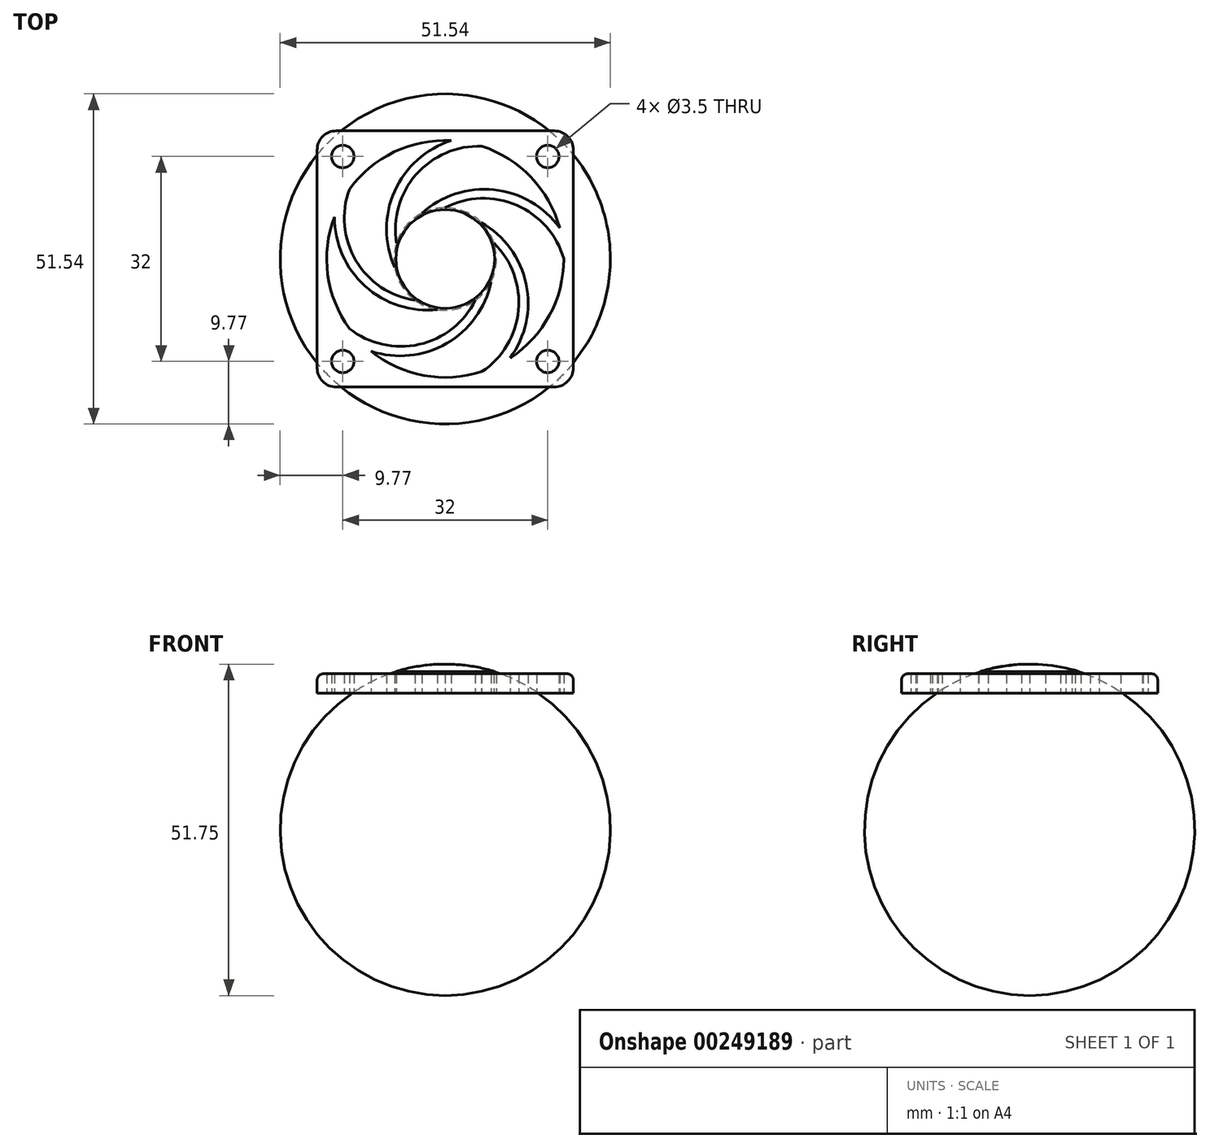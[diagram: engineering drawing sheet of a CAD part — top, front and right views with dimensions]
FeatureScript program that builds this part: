
annotation { "Feature Type Name" : "Feature", "Feature Type Description" : "" }
export const myFeature = defineFeature(function(context is Context, id is Id, definition is map)
    precondition{}
    {
        {
            var Q0;
            Q0=qCreatedBy(makeId("Top.planeOp"),FACE);
            var sketch = newSketch(context, id + "F0", { "sketchPlane" : qUnion([Q0])});
            skLineSegment(sketch, "E0.bottom", {"start": v(3, 0) * mm, "end": v(37, 0) * mm});
            skLineSegment(sketch, "E0.top", {"start": v(3, 40) * mm, "end": v(37, 40) * mm});
            skLineSegment(sketch, "E0.left", {"start": v(0, 3) * mm, "end": v(0, 37) * mm});
            skLineSegment(sketch, "E0.right", {"start": v(40, 3) * mm, "end": v(40, 37) * mm});
            skPoint(sketch, "E1.visualSharp", {"position": v(0, 40) * mm});
            skArc(sketch, "E1.filletArc", {"start": v(3, 40) * mm, "mid": v(0.88, 39.12) * mm, "end": v(0, 37) * mm});
            skPoint(sketch, "E2.visualSharp", {"position": v(40, 0) * mm});
            skArc(sketch, "E2.filletArc", {"start": v(37, 0) * mm, "mid": v(39.12, 0.88) * mm, "end": v(40, 3) * mm});
            skPoint(sketch, "E3.visualSharp", {"position": v(0, 0) * mm});
            skArc(sketch, "E3.filletArc", {"start": v(0, 3) * mm, "mid": v(0.88, 0.88) * mm, "end": v(3, 0) * mm});
            skLineSegment(sketch, "E4.bottom", {"start": v(4, 36) * mm, "end": v(36, 36) * mm, "construction": true});
            skLineSegment(sketch, "E4.top", {"start": v(4, 4) * mm, "end": v(36, 4) * mm, "construction": true});
            skLineSegment(sketch, "E4.left", {"start": v(4, 36) * mm, "end": v(4, 4) * mm, "construction": true});
            skLineSegment(sketch, "E4.right", {"start": v(36, 36) * mm, "end": v(36, 4) * mm, "construction": true});
            skLineSegment(sketch, "E5", {"start": v(20, 40) * mm, "end": v(20, 0) * mm, "construction": true});
            skArc(sketch, "E6", {"start": v(37.86, 24.83) * mm, "mid": v(33.4, 32.75) * mm, "end": v(25.72, 37.6) * mm});
            skArc(sketch, "E7", {"start": v(16.33, 27.11) * mm, "mid": v(13.9, 25.18) * mm, "end": v(12.4, 22.47) * mm});
            skCircle(sketch, "E8", {"center": v(4, 36) * mm, "radius": 1.75 * mm});
            skCircle(sketch, "E9", {"center": v(36, 36) * mm, "radius": 1.75 * mm});
            skCircle(sketch, "E10", {"center": v(36, 4) * mm, "radius": 1.75 * mm});
            skCircle(sketch, "E11", {"center": v(4, 4) * mm, "radius": 1.75 * mm});
            skLineSegment(sketch, "E12", {"start": v(20, 20) * mm, "end": v(38.5, 20) * mm, "construction": true});
            skArc(sketch, "E13", {"start": v(38.5, 20) * mm, "mid": v(31.15, 28.4) * mm, "end": v(20, 28) * mm});
            skArc(sketch, "E14.trimOffspring", {"start": v(37.86, 24.83) * mm, "mid": v(27.6, 30.8) * mm, "end": v(16.33, 27.11) * mm});
            skLineSegment(sketch, "E15", {"start": v(16.33, 27.11) * mm, "end": v(20, 20) * mm, "construction": true});
            skLineSegment(sketch, "E16", {"start": v(37.86, 24.83) * mm, "end": v(20, 20) * mm, "construction": true});
            skArc(sketch, "E17.1.0", {"start": v(25.72, 37.6) * mm, "mid": v(15.46, 33.2) * mm, "end": v(12.4, 22.47) * mm});
            skArc(sketch, "E17.1.1", {"start": v(20.92, 38.48) * mm, "mid": v(12.08, 30.57) * mm, "end": v(12.1, 18.71) * mm});
            skArc(sketch, "E17.2.0", {"start": v(5.03, 30.87) * mm, "mid": v(6.04, 19.76) * mm, "end": v(15.3, 13.53) * mm});
            skArc(sketch, "E17.2.1", {"start": v(2.71, 26.59) * mm, "mid": v(7.5, 15.74) * mm, "end": v(18.79, 12.1) * mm});
            skArc(sketch, "E17.3.0", {"start": v(5.03, 9.13) * mm, "mid": v(15.91, 6.65) * mm, "end": v(24.7, 13.53) * mm});
            skArc(sketch, "E17.3.1", {"start": v(8.4, 5.6) * mm, "mid": v(20.2, 6.8) * mm, "end": v(27.15, 16.4) * mm});
            skArc(sketch, "E17.4.0", {"start": v(25.72, 2.4) * mm, "mid": v(31.43, 11.99) * mm, "end": v(27.6, 22.47) * mm});
            skArc(sketch, "E17.4.1", {"start": v(30.11, 4.51) * mm, "mid": v(32.62, 16.1) * mm, "end": v(25.63, 25.68) * mm});
            skArc(sketch, "E18.trimOffspring", {"start": v(12.1, 18.71) * mm, "mid": v(13.19, 15.8) * mm, "end": v(15.3, 13.53) * mm});
            skArc(sketch, "E19.trimOffspring", {"start": v(18.79, 12.1) * mm, "mid": v(21.89, 12.23) * mm, "end": v(24.7, 13.53) * mm});
            skArc(sketch, "E20.trimOffspring", {"start": v(27.15, 16.4) * mm, "mid": v(27.98, 19.4) * mm, "end": v(27.6, 22.47) * mm});
            skArc(sketch, "E21.trimOffspring", {"start": v(25.63, 25.68) * mm, "mid": v(23.04, 27.4) * mm, "end": v(20, 28) * mm});
            skArc(sketch, "E22.trimOffspring", {"start": v(20.92, 38.48) * mm, "mid": v(12.01, 36.69) * mm, "end": v(5.03, 30.87) * mm});
            skArc(sketch, "E23.trimOffspring", {"start": v(2.71, 26.59) * mm, "mid": v(1.66, 17.56) * mm, "end": v(5.03, 9.13) * mm});
            skArc(sketch, "E24.trimOffspring", {"start": v(30.11, 4.51) * mm, "mid": v(36.27, 11.2) * mm, "end": v(38.5, 20) * mm});
            skArc(sketch, "E25.trimOffspring", {"start": v(8.4, 5.6) * mm, "mid": v(16.65, 1.8) * mm, "end": v(25.72, 2.4) * mm});
            skPoint(sketch, "E26.visualSharp", {"position": v(40, 40) * mm});
            skArc(sketch, "E26.filletArc", {"start": v(40, 37) * mm, "mid": v(39.12, 39.12) * mm, "end": v(37, 40) * mm});
            skSolve(sketch);
        }
        {
            var Q0;
            Q0=qSketchRegion(id+"F0",true);
            extrude(context, id + "F1", {"entities" : qUnion([Q0]), "depth" : 3 * mm});
        }
        {
            var Q0;
            Q0=makeQuery(id+"F1.opExtrude","CAP_EDGE",EDGE,{"disambiguationData":[OSD([sQuery(id+"F0.wireOp",EDGE,"E0.bottom")])],"isStart":false});
            fillet(context, id + "F2", {"entities" : qUnion([Q0]), "radius" : 1 * mm, "tangentPropagation" : true, "allowEdgeOverflow" : false});
        }
        {
            var Q0;
            Q0=makeQuery(id+"F1.opExtrude","SWEPT_FACE",FACE,{"disambiguationData":[OSD([sQuery(id+"F0.wireOp",EDGE,"E0.bottom")])]});
            cPlane(context, id + "F3", {"entities" : qUnion([Q0]), "cplaneType" : CPlaneType.OFFSET, "offset" : 20 * mm, "oppositeDirection" : true, "width" : 150 * mm, "height" : 150 * mm});
        }
        {
            var Q0;
            Q0=qCreatedBy(id+"F3.planeOp",FACE);
            var sketch = newSketch(context, id + "F4", { "sketchPlane" : qUnion([Q0])});
            skLineSegment(sketch, "E27", {"start": v(0, 0) * mm, "end": v(20, 0) * mm, "construction": true});
            skLineSegment(sketch, "E28", {"start": v(20, 0) * mm, "end": v(20, 4.5) * mm, "construction": true});
            skLineSegment(sketch, "E29", {"start": v(20, 3) * mm, "end": v(12, 3) * mm});
            skLineSegment(sketch, "E30", {"start": v(20, 4.5) * mm, "end": v(23, 4.49) * mm, "construction": true});
            skLineSegment(sketch, "E31", {"start": v(20, 4.5) * mm, "end": v(20, 3) * mm});
            skArc(sketch, "E32", {"start": v(12.3, 3.36) * mm, "mid": v(12.1, 3.22) * mm, "end": v(12, 3) * mm});
            skArc(sketch, "E33", {"start": v(20, 4.5) * mm, "mid": v(16.1, 4.22) * mm, "end": v(12.3, 3.36) * mm});
            skSolve(sketch);
        }
        {
            var Q0;
            Q0=qSketchRegion(id+"F4",true);
            var Q1;
            Q1=sQuery(id+"F4.wireOp",EDGE,"E28");
            revolve(context, id + "F5", {"operationType" : NewBodyOperationType.ADD, "entities" : qUnion([Q0]), "axis" : qUnion([Q1]), "revolveType" : RevolveType.FULL});
        }
    });
